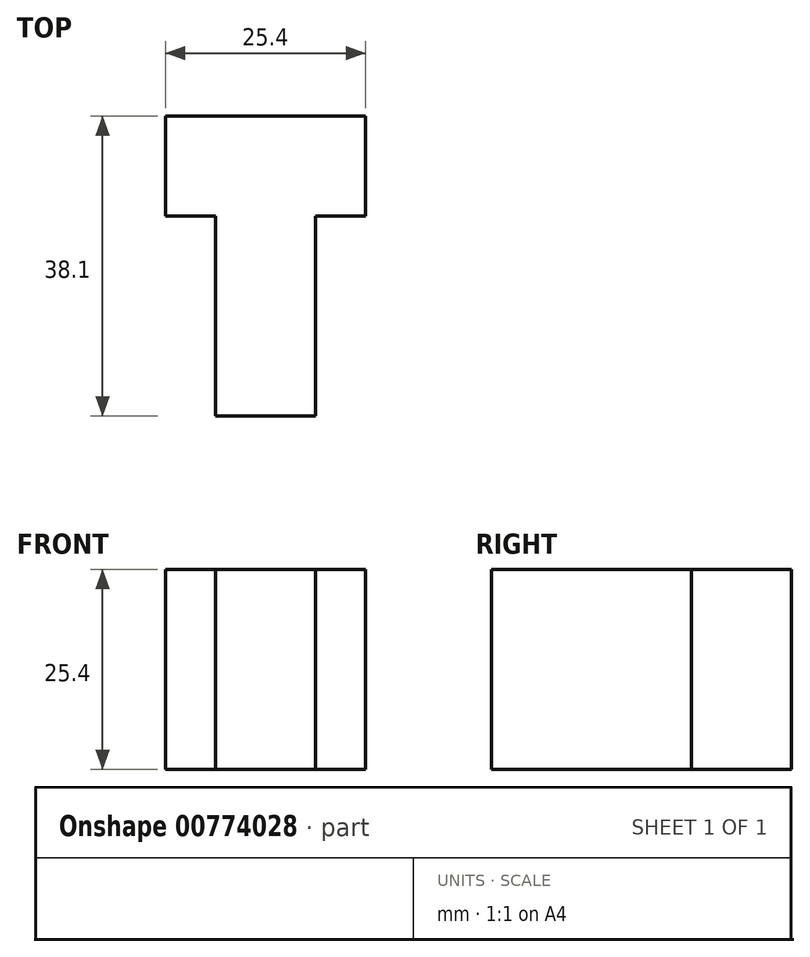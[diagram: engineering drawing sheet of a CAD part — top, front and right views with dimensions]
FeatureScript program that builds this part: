
annotation { "Feature Type Name" : "Feature", "Feature Type Description" : "" }
export const myFeature = defineFeature(function(context is Context, id is Id, definition is map)
    precondition{}
    {
        {
            var Q0;
            Q0=qCreatedBy(makeId("Top.planeOp"),FACE);
            var sketch = newSketch(context, id + "F0", { "sketchPlane" : qUnion([Q0])});
            skLineSegment(sketch, "E0", {"start": v(0, 0) * mm, "end": v(-25.4, 0) * mm});
            skLineSegment(sketch, "E1", {"start": v(-25.4, 0) * mm, "end": v(-25.4, -12.7) * mm});
            skLineSegment(sketch, "E2", {"start": v(-25.4, -12.7) * mm, "end": v(-19.05, -12.7) * mm});
            skLineSegment(sketch, "E3", {"start": v(-19.05, -12.7) * mm, "end": v(-19.05, -38.1) * mm});
            skLineSegment(sketch, "E4", {"start": v(-19.05, -38.1) * mm, "end": v(-6.35, -38.1) * mm});
            skLineSegment(sketch, "E5", {"start": v(-6.35, -38.1) * mm, "end": v(-6.35, -12.7) * mm});
            skLineSegment(sketch, "E6", {"start": v(0, 0) * mm, "end": v(0, -12.7) * mm});
            skLineSegment(sketch, "E7", {"start": v(0, -12.7) * mm, "end": v(-6.35, -12.7) * mm});
            skSolve(sketch);
        }
        {
            var Q0;
            Q0 = qSketchRegion(id + "F0", true);
            extrude(context, id + "F1", {"entities" : qUnion([Q0]), "depth" : 25.4 * mm, "offsetDistance" : 25.4 * mm});
        }
    });
